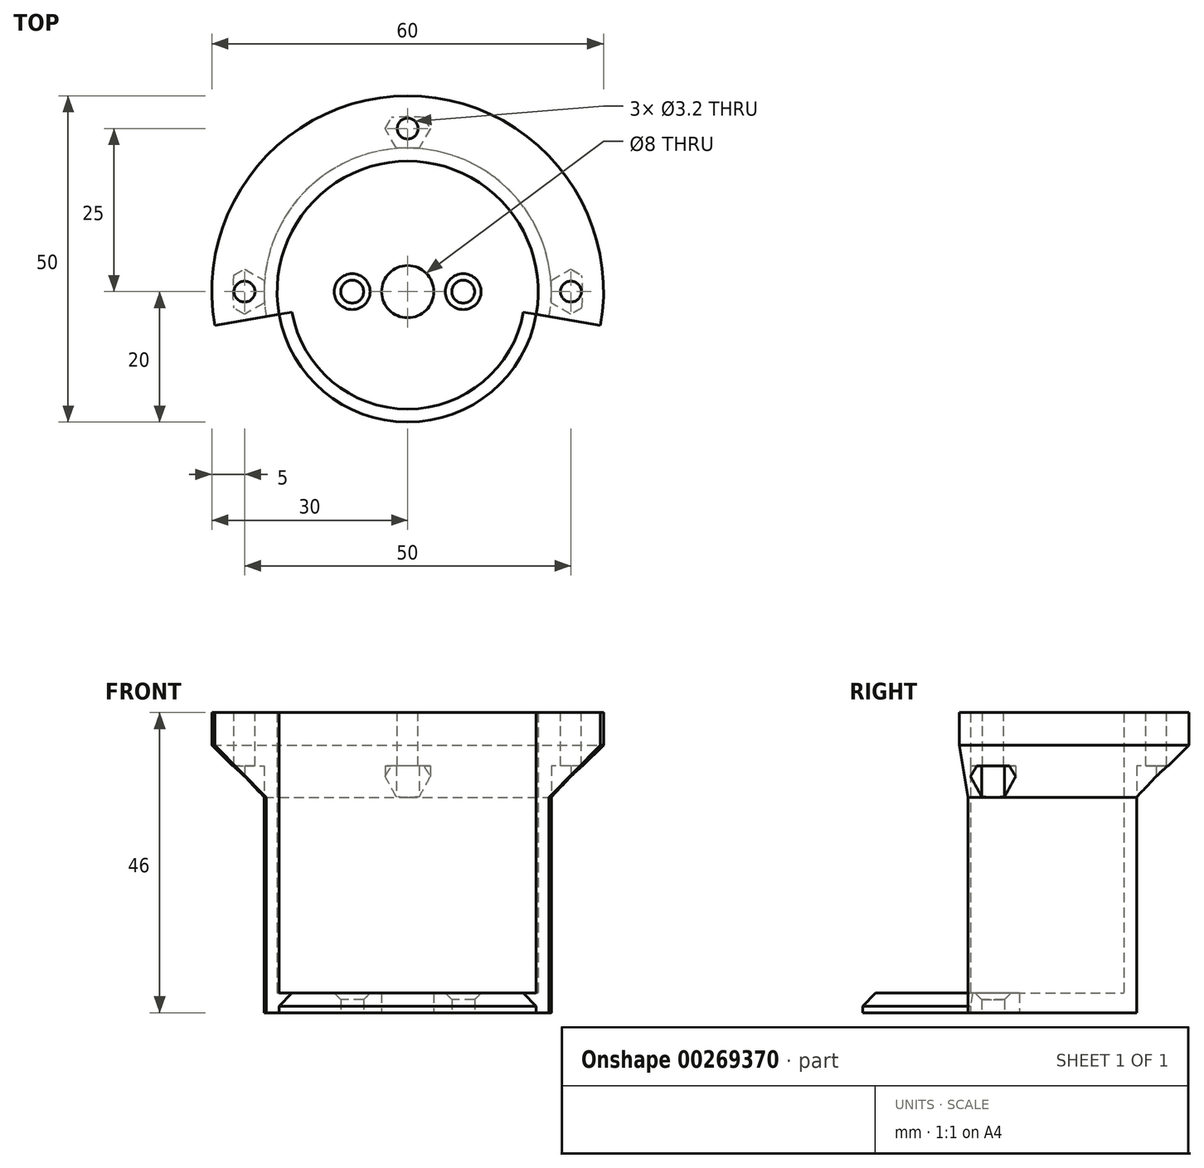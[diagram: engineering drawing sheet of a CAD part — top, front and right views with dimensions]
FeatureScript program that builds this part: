
annotation { "Feature Type Name" : "Feature", "Feature Type Description" : "" }
export const myFeature = defineFeature(function(context is Context, id is Id, definition is map)
    precondition{}
    {
        {
            var Q0;
            Q0=qCreatedBy(makeId("Top.planeOp"),FACE);
            var sketch = newSketch(context, id + "F0", { "sketchPlane" : qUnion([Q0])});
            skCircle(sketch, "E0", {"center": v(0, 0) * mm, "radius": 20 * mm});
            skLineSegment(sketch, "E1", {"start": v(-8.5, 0) * mm, "end": v(8.5, 0) * mm});
            skCircle(sketch, "E2", {"center": v(-8.5, 0) * mm, "radius": 1.75 * mm});
            skCircle(sketch, "E3", {"center": v(8.5, 0) * mm, "radius": 1.75 * mm});
            skCircle(sketch, "E4", {"center": v(0, 0) * mm, "radius": 4 * mm});
            skSolve(sketch);
        }
        {
            var Q0;
            Q0 = qSketchRegion(id + "F0", true);
            extrude(context, id + "F1", {"entities" : qUnion([Q0]), "depth" : 3 * mm});
        }
        {
            var Q0;
            Q0=makeQuery(id+"F1.opExtrude","CAP_EDGE",EDGE,{"disambiguationData":[OSD([sQuery(id+"F0.wireOp",EDGE,"E2")])],"isStart":false});
            var Q1;
            Q1=makeQuery(id+"F1.opExtrude","CAP_EDGE",EDGE,{"disambiguationData":[OSD([sQuery(id+"F0.wireOp",EDGE,"E3")])],"isStart":false});
            chamfer(context, id + "F2", {"entities" : qUnion([Q0, Q1]), "width" : 1 * mm, "tangentPropagation" : true});
        }
        {
            var Q0;
            Q0=qCreatedBy(makeId("Top.planeOp"),FACE);
            var sketch = newSketch(context, id + "F3", { "sketchPlane" : qUnion([Q0])});
            skArc(sketch, "E5", {"start": v(21.67, -3.82) * mm, "mid": v(0, 22) * mm, "end": v(-21.67, -3.82) * mm});
            skArc(sketch, "E6", {"start": v(19.7, -3.47) * mm, "mid": v(0, 20) * mm, "end": v(-19.7, -3.47) * mm});
            skLineSegment(sketch, "E7", {"start": v(0, 0) * mm, "end": v(0, -20.97) * mm});
            skLineSegment(sketch, "E8", {"start": v(-19.7, -3.47) * mm, "end": v(-21.67, -3.82) * mm});
            skLineSegment(sketch, "E9", {"start": v(19.7, -3.47) * mm, "end": v(21.67, -3.82) * mm});
            skSolve(sketch);
        }
        {
            var Q0;
            Q0 = qSketchRegion(id + "F3", true);
            extrude(context, id + "F4", {"entities" : qUnion([Q0]), "operationType" : NewBodyOperationType.ADD, "depth" : 46 * mm});
        }
        {
            var Q0;
            {var subQ0=sQuery(id+"F0.wireOp",EDGE,"E0");Q0=makeQuery(id+"F4.boolean.opBoolean","SPLIT",EDGE,{"disambiguationData":[topologyDisambiguationEdgeConnected([makeQuery(id+"F4.opExtrude","SWEPT_FACE",FACE,{"disambiguationData":[OSD([sQuery(id+"F3.wireOp",EDGE,"E6")])]})])],"derivedFrom":makeQuery(id+"F1.opExtrude","CAP_EDGE",EDGE,{"disambiguationData":[OSD([subQ0])],"isStart":false})});}
            chamfer(context, id + "F5", {"entities" : qUnion([Q0]), "width" : 2 * mm, "tangentPropagation" : true});
        }
        {
            var Q0;
            Q0=makeQuery(id+"F4.opExtrude","CAP_FACE",FACE,{"disambiguationData":[OSD([sQuery(id+"F3.wireOp",EDGE,"E5"),sQuery(id+"F3.wireOp",EDGE,"E6"),sQuery(id+"F3.wireOp",EDGE,"E8"),sQuery(id+"F3.wireOp",EDGE,"E9")])],"isStart":false});
            cPlane(context, id + "F6", {"entities" : qUnion([Q0]), "cplaneType" : CPlaneType.OFFSET, "offset" : 0 * mm, "width" : 150 * mm, "height" : 150 * mm});
        }
        {
            var Q0;
            Q0=qCreatedBy(makeId("Right.planeOp"),FACE);
            var sketch = newSketch(context, id + "F7", { "sketchPlane" : qUnion([Q0])});
            skLineSegment(sketch, "E10", {"start": v(0, 0) * mm, "end": v(22, 0) * mm});
            skLineSegment(sketch, "E11", {"start": v(22, 0) * mm, "end": v(22, 33) * mm});
            skLineSegment(sketch, "E12", {"start": v(22, 33) * mm, "end": v(30, 41) * mm});
            skLineSegment(sketch, "E13", {"start": v(30, 41) * mm, "end": v(30, 46) * mm});
            skLineSegment(sketch, "E14", {"start": v(30, 46) * mm, "end": v(22, 46) * mm});
            skLineSegment(sketch, "E15", {"start": v(22, 46) * mm, "end": v(22, 33) * mm});
            skLineSegment(sketch, "E16", {"start": v(0, -27.2) * mm, "end": v(0, 53.76) * mm});
            skSolve(sketch);
        }
        {
            var Q0;
            Q0=makeQuery(id+"F7.imprint","IMPRINT",FACE,{"disambiguationData":[TD([[makeQuery(id+"F7.imprint","IMPRINT",EDGE,{"derivedFrom":sQuery(id+"F7.wireOp",EDGE,"E12")}),1.0]])]});
            var Q1;
            Q1=sQuery(id+"F7.wireOp",EDGE,"E16");
            revolve(context, id + "F8", {"operationType" : NewBodyOperationType.ADD, "entities" : qUnion([Q0]), "axis" : qUnion([Q1]), "revolveType" : RevolveType.SYMMETRIC, "angle" : 200 * degree});
        }
        {
            var Q0;
            Q0=qCreatedBy(id+"F6.planeOp",FACE);
            var sketch = newSketch(context, id + "F9", { "sketchPlane" : qUnion([Q0])});
            skLineSegment(sketch, "E17", {"start": v(0, 0) * mm, "end": v(0, 25) * mm});
            skCircle(sketch, "E18", {"center": v(0, 25) * mm, "radius": 1.6 * mm});
            skCircle(sketch, "E19.1.0", {"center": v(-25, 0) * mm, "radius": 1.6 * mm});
            skCircle(sketch, "E19.3.0", {"center": v(25, 0) * mm, "radius": 1.6 * mm});
            skPoint(sketch, "E19.center", {"position": v(0, 0) * mm});
            skSolve(sketch);
        }
        {
            var Q0;
            Q0 = qSketchRegion(id + "F9", true);
            extrude(context, id + "F10", {"entities" : qUnion([Q0]), "operationType" : NewBodyOperationType.REMOVE, "oppositeDirection" : true, "depth" : 25 * mm});
        }
        {
            var Q0;
            Q0=qCreatedBy(makeId("Top.planeOp"),FACE);
            var sketch = newSketch(context, id + "F11", { "sketchPlane" : qUnion([Q0])});
            skLineSegment(sketch, "E20", {"start": v(0, 0) * mm, "end": v(0, 25) * mm});
            skCircle(sketch, "E21.cCircle", {"center": v(0, 25) * mm, "radius": 3 * mm, "construction": true});
            skLineSegment(sketch, "E21.0", {"start": v(1.73, 22) * mm, "end": v(-1.73, 22) * mm});
            skLineSegment(sketch, "E21.1", {"start": v(-1.73, 22) * mm, "end": v(-3.46, 25) * mm});
            skLineSegment(sketch, "E21.2", {"start": v(-3.46, 25) * mm, "end": v(-1.73, 28) * mm});
            skLineSegment(sketch, "E21.3", {"start": v(-1.73, 28) * mm, "end": v(1.73, 28) * mm});
            skLineSegment(sketch, "E21.4", {"start": v(1.73, 28) * mm, "end": v(3.46, 25) * mm});
            skLineSegment(sketch, "E21.5", {"start": v(3.46, 25) * mm, "end": v(1.73, 22) * mm});
            skPoint(sketch, "E21.0.midPoint", {"position": v(0, 22) * mm});
            skLineSegment(sketch, "E22.1.0", {"start": v(-22, 1.73) * mm, "end": v(-22, -1.73) * mm});
            skCircle(sketch, "E22.1.1", {"center": v(-25, 0) * mm, "radius": 3 * mm, "construction": true});
            skPoint(sketch, "E22.1.2", {"position": v(-22, 0) * mm});
            skLineSegment(sketch, "E22.1.3", {"start": v(-25, 3.46) * mm, "end": v(-22, 1.73) * mm});
            skLineSegment(sketch, "E22.1.4", {"start": v(-28, 1.73) * mm, "end": v(-25, 3.46) * mm});
            skLineSegment(sketch, "E22.1.5", {"start": v(-22, -1.73) * mm, "end": v(-25, -3.46) * mm});
            skLineSegment(sketch, "E22.1.6", {"start": v(-28, -1.73) * mm, "end": v(-28, 1.73) * mm});
            skLineSegment(sketch, "E22.1.7", {"start": v(-25, -3.46) * mm, "end": v(-28, -1.73) * mm});
            skLineSegment(sketch, "E22.3.0", {"start": v(22, -1.73) * mm, "end": v(22, 1.73) * mm});
            skCircle(sketch, "E22.3.1", {"center": v(25, 0) * mm, "radius": 3 * mm, "construction": true});
            skPoint(sketch, "E22.3.2", {"position": v(22, 0) * mm});
            skLineSegment(sketch, "E22.3.3", {"start": v(25, -3.46) * mm, "end": v(22, -1.73) * mm});
            skLineSegment(sketch, "E22.3.4", {"start": v(28, -1.73) * mm, "end": v(25, -3.46) * mm});
            skLineSegment(sketch, "E22.3.5", {"start": v(22, 1.73) * mm, "end": v(25, 3.46) * mm});
            skLineSegment(sketch, "E22.3.6", {"start": v(28, 1.73) * mm, "end": v(28, -1.73) * mm});
            skLineSegment(sketch, "E22.3.7", {"start": v(25, 3.46) * mm, "end": v(28, 1.73) * mm});
            skPoint(sketch, "E22.center", {"position": v(0, 0) * mm});
            skSolve(sketch);
        }
        {
            var Q0;
            Q0 = qSketchRegion(id + "F11", true);
            extrude(context, id + "F12", {"entities" : qUnion([Q0]), "operationType" : NewBodyOperationType.REMOVE, "depth" : 37.8 * mm});
        }
    });
